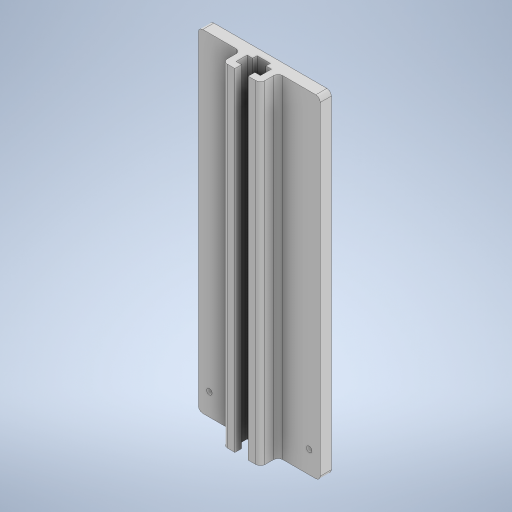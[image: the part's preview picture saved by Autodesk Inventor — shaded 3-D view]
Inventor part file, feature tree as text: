
AUTODESK INVENTOR PART (.ipt)
format: ipt  version: 2024.3 (Build 283343010, 343A)  size: 282,624 bytes
history: native  units: mm
features: sketch x4, extrude x3, other x1, hole x1, fillet x1, projected_geometry x1
ambient origin geometry x8: Origin, YZ Plane, XZ Plane, XY Plane, X Axis, Y Axis, Z Axis, Center Point
bodies: Body1 (feature_tree)
feature tree (11):
  other  "ソリッド1"
  extrude  "押し出し1"  Depth=55.0mm
  extrude  "押し出し2"  Depth=150.0mm
  extrude  "押し出し3"  Depth=5.0mm TaperAngle=0.0deg
  hole  "穴1"  [1 undecoded]
  fillet  "フィレット1"  Radius=8.0mm
  sketch  "スケッチ1"
  sketch  "スケッチ2"
  sketch  "スケッチ3"
  projected_geometry  "投影ループ1"
  sketch  "スケッチ4"
note: 1 required parameter value undecoded (feature->parameter linkage not recoverable at this tier; creation-order binding heuristic only, values carry confidence <= 0.55)
